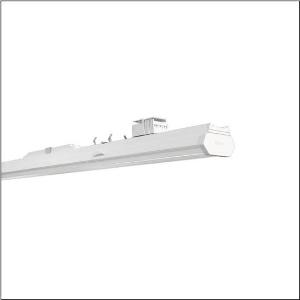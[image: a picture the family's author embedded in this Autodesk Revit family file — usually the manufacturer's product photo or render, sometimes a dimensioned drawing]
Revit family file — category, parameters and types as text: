
# Revit family: licross_r__21_protected_ho_52td12dn4axm_e376
name_source: partatom
category: Lighting Fixtures
units: mm (PartAtom-declared; Revit-internal decimal feet)

## family parameters
Cut with Voids When Loaded = No
Host = Face
Light Source = No
Part Type = Normal
Room Calculation Point = No
Round Connector Dimension = Use Diameter
Shared = No

## types (1)
- --- (1 x LED, 10000 lm, 56 W, 4000K)
    Apparent Load = 56 VA
    CIE Flux Codes = 70 91 97 98 100
    Color Rendering = 80
    Color Temperature = 4000K
    Default Elevation = 1800 mm
    Description = Licross® 21 Protected HO, luminaire insert, of sheet steel, galvanised, coil coated, white, length: 1.500mm, width: 90mm, height: 103mm, LED rated luminous flux: 10.000lm, light colour: 840, control gear: DALI 2, with plug, 5-pole, with phase selection, mains connection: 220..240V, AC, 50/60Hz, rated input power: 56W, halogen-free wiring, primary light control with lens, of plastic, primary optical cover: cover, of PMMA, light emission: direct distribution, primary light characteristic: symmetric, protection rating (complete): IP54, insulation class (complete): insulation class I (protective earthing), certification: CE, ENEC, VDE, UKCA, protection symbol: D if used in an environment with non-conductive dust loads with corresponding accessories, impact resistance: IK06, permissible ambient temperature for indoor applications: -25..+45°C, corresponds to IFS (International Featured Standards) requirements for safety and quality in the food industry, reducing of maximum allowable ambient temperature of 5°C with ceiling mounting, LABS conformity tested according to VDMA 24364:2018-05, packaging unit: 1 piece
    Height = 92 mm
    Lamp = 1 x LED
    Lamp Light Flux = 10000 lm
    Lamp Power = 56 W
    Lamp count = 1
    Length = 1500 mm
    Luminous efficacy = 179 lm/W
    Manufacturer = Siteco
    ModVariant = No
    Model = 52TD12DN4AXM
    Mounting Place = Ceiling
    Mounting Type = Pendant
    Number of Poles = 1
    OnlyDefault = Yes
    Power Factor = 1
    Product Name = Licross® 21 Protected HO
    Product group = luminaire insert
    ProductGroupID = 901
    Protection Class = Protection class I
    Protection Degree = IP 54
    RLX_Detail_Level = 1
    RLX_Emergency_Light_Flux = 0 lm
    RLX_Emergency_Type = 0
    RLX_Emergency_Type_DB = No
    RlxData = <blob elided: 24117 chars, md5=36c85e70>
    Socket = socket
    Standby Power = 0 W
    System Light Flux = 10000 lm
    System Power = 56 W
    Type Comments = factory setting: luminous flux: 100 % | dim-lin: 254 | 321 mA
    Type Image = l_1256148.jpg
    URL = http://relux.com
    VarID = @adj_078663
    Voltage = 0 V
    Weight = 0.00 kg
    Width = 88 mm

## geometry (parser evidence)
native form markers: Blend x4, Sweep x11
no freeform markers — native parametric forms only
